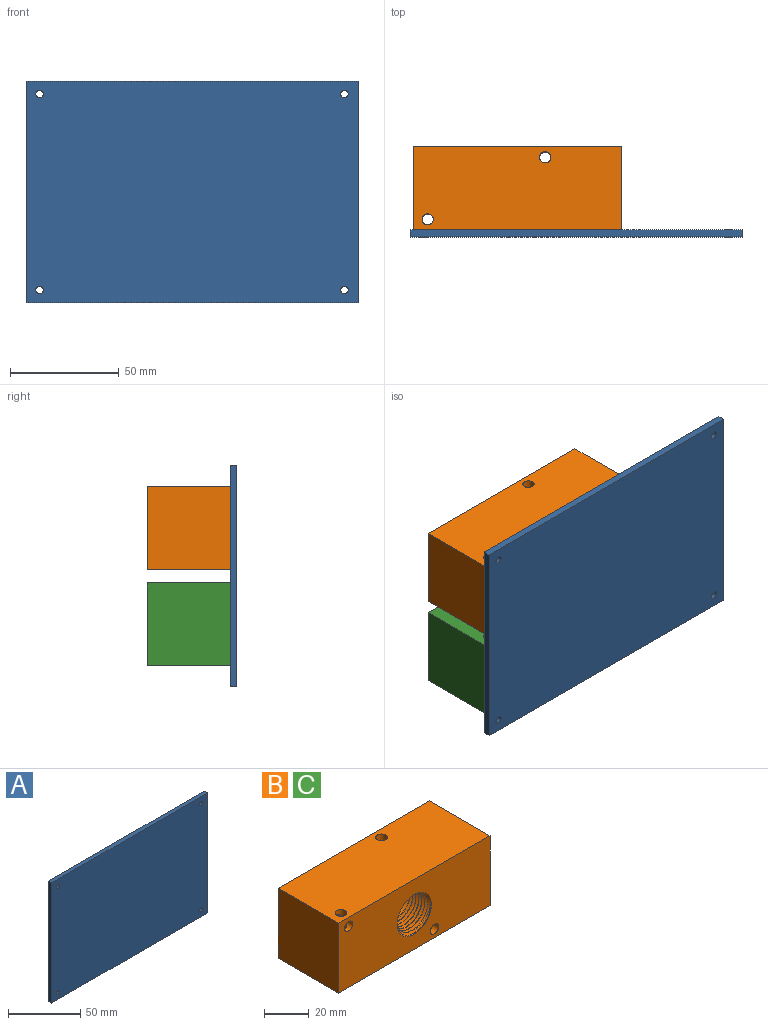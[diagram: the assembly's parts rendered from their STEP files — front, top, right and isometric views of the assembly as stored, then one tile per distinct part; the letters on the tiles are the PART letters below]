
ASSEMBLY  parts=3 mates=1
PART A: 10 faces, bbox 152.4x3.2x101.6 mm
  f0: plane 101.6x3.18mm, normal (1,0,0), area 322.6mm2, adj f1,f3,f4,f5
  f1: plane 152.4x3.18mm, normal (0,0,1), area 483.9mm2, adj f0,f2,f4,f5
  f2: plane 101.6x3.18mm, normal (-1,0,0), area 322.6mm2, adj f1,f3,f4,f5
  f3: plane 152.4x3.18mm, normal (0,0,-1), area 483.9mm2, adj f0,f2,f4,f5
  f4: plane 152.4x101.6mm, normal (0,-1,0), area 15446.4mm2, adj f0,f1,f2,f3,f6,f7,f8,f9
  f5: plane 152.4x101.6mm, normal (0,1,0), area 15446.4mm2, adj f0,f1,f2,f3,f6,f7,f8,f9
  f6: cylinder r=1.73mm len=3.45mm, axis (0,-1,0), area 34.5mm2, adj f4,f5
  f7: cylinder r=1.73mm len=3.45mm, axis (0,-1,0), area 34.5mm2, adj f4,f5
  f8: cylinder r=1.73mm len=3.45mm, axis (0,-1,0), area 34.5mm2, adj f4,f5
  f9: cylinder r=1.73mm len=3.45mm, axis (0,-1,0), area 34.5mm2, adj f4,f5
PART B: 53 faces, bbox 95.3x39.1x38.1 mm
  f0: cylinder r=4.3mm len=8.69mm, axis (0,1,0), area 197.8mm2, adj f17,f36,f52
  f1: cylinder r=4.3mm len=8.69mm, axis (0,1,0), area 160.9mm2, adj f11,f17,f51
  f2: cone r=8.3mm half-angle=45deg, axis (0,1,0), area 57.6mm2, adj f3,f49,f50,f51
  f3: cone r=8.57mm half-angle=1.8deg, axis (0,1,0), area 20.8mm2, adj f2,f4,f49,f50
  f4: cone r=8.83mm half-angle=45deg, axis (0,1,0), area 56.5mm2, adj f3,f5,f35,f49,f50
  f5: cone r=8.83mm half-angle=45deg, axis (0,1,0), area 5.4mm2, adj f4,f49,f50
  f6: cone r=10.79mm half-angle=45deg, axis (0,-1,0), area 58.4mm2, adj f7,f9,f33,f47,f48
  f7: cone r=10.79mm half-angle=45deg, axis (0,-1,0), area 11.3mm2, adj f6,f46,f47,f48
  f8: cone r=10.3mm half-angle=45deg, axis (0,-1,0), area 100.7mm2, adj f9,f45,f46,f47,f48
  f9: cone r=10.67mm half-angle=1.8deg, axis (0,-1,0), area 83mm2, adj f6,f8,f47,f48
  f10: cylinder r=5.89mm len=11.79mm, axis (0,-1,0), area 140.4mm2, adj f11,f17,f43,f44,f45
  f11: cylinder r=4.3mm len=25.4mm, axis (-1,0,0), area 545.2mm2, adj f1,f10,f16,f42,f43,f44
  f12: cone r=8.83mm half-angle=45deg, axis (0,1,0), area 56.5mm2, adj f13,f15,f35,f40,f41
  f13: cone r=8.83mm half-angle=45deg, axis (0,1,0), area 5.4mm2, adj f12,f40,f41
  f14: cone r=8.3mm half-angle=45deg, axis (0,1,0), area 57.6mm2, adj f15,f39,f40,f41
  f15: cone r=8.57mm half-angle=1.8deg, axis (0,1,0), area 20.8mm2, adj f12,f14,f40,f41
  f16: cylinder r=4.3mm len=8.69mm, axis (0,1,0), area 197.8mm2, adj f11,f39,f42
  f17: cylinder r=4.3mm len=25.4mm, axis (-1,0,0), area 545.2mm2, adj f0,f1,f10,f43,f44,f52
  f18: cone r=8.83mm half-angle=45deg, axis (0,1,0), area 56.5mm2, adj f19,f21,f35,f37,f38
  f19: cone r=8.83mm half-angle=45deg, axis (0,1,0), area 5.4mm2, adj f18,f37,f38
  f20: cone r=8.3mm half-angle=45deg, axis (0,1,0), area 57.6mm2, adj f21,f36,f37,f38
  f21: cone r=8.57mm half-angle=1.8deg, axis (0,1,0), area 20.8mm2, adj f18,f20,f37,f38
  f22: cylinder r=2.58mm len=5.16mm, axis (0,1,0), area 57.3mm2, adj f27,f29,f35
  f23: cylinder r=2.58mm len=33.27mm, axis (0,1,0), area 518.1mm2, adj f27,f29,f33
  f24: cylinder r=2.58mm len=33.27mm, axis (0,1,0), area 518.1mm2, adj f26,f28,f35
  f25: cylinder r=2.58mm len=5.16mm, axis (0,1,0), area 57.3mm2, adj f26,f28,f33
  f26: cylinder r=2.58mm len=33.27mm, axis (0,0,-1), area 518.1mm2, adj f24,f25,f31
  f27: cylinder r=2.58mm len=5.16mm, axis (0,0,-1), area 57.3mm2, adj f22,f23,f31
  f28: cylinder r=2.58mm len=5.16mm, axis (0,0,-1), area 57.3mm2, adj f24,f25,f30
  f29: cylinder r=2.58mm len=33.27mm, axis (0,0,-1), area 518.1mm2, adj f22,f23,f30
  f30: plane 95.25x38.1mm, normal (0,0,1), area 3587.3mm2, adj f28,f29,f32,f33,f34,f35
  f31: plane 95.25x38.1mm, normal (0,0,-1), area 3587.3mm2, adj f26,f27,f32,f33,f34,f35
  f32: plane 38.1x38.1mm, normal (-1,0,0), area 1451.6mm2, adj f30,f31,f33,f35
  f33: plane 95.25x38.1mm, normal (0,-1,0), area 3221.2mm2, adj f6,f23,f25,f30,f31,f32,f34
  f34: plane 38.1x38.1mm, normal (1,0,0), area 1451.6mm2, adj f30,f31,f33,f35
  f35: plane 95.25x38.1mm, normal (0,1,0), area 2853mm2, adj f4,f12,f18,f22,f24,f30,f31,f32
  f36: plane 13.68x13.68mm, normal (0,1,0), area 88.9mm2, adj f0,f20
  f37: bspline ~17x16.91mm, area 398.5mm2, adj f18,f19,f20,f21,f38
  f38: bspline ~16.9x16.84mm, area 413.1mm2, adj f18,f19,f20,f21,f37
  f39: plane 13.68x13.68mm, normal (0,1,0), area 88.9mm2, adj f14,f16
  f40: bspline ~17x16.91mm, area 398.5mm2, adj f12,f13,f14,f15,f41
  f41: bspline ~16.9x16.84mm, area 413.1mm2, adj f12,f13,f14,f15,f40
  f42: sphere r=4.3mm, area 58.1mm2, adj f11,f16
  f43: plane 8.06x1.59mm, normal (0,-1,0), area 8.8mm2, adj f10,f11,f17
  f44: plane 8.06x1.59mm, normal (0,-1,0), area 8.8mm2, adj f10,f11,f17
  f45: plane 16.87x16.87mm, normal (0,-1,0), area 114.3mm2, adj f8,f10
  f46: bspline ~18.57x18.55mm, area 83.9mm2, adj f7,f8,f47,f48
  f47: bspline ~21.51x21.51mm, area 537.3mm2, adj f6,f7,f8,f9,f46
  f48: bspline ~21.6x21.59mm, area 560mm2, adj f6,f7,f8,f9,f46
  f49: bspline ~16.9x16.84mm, area 413.1mm2, adj f2,f3,f4,f5,f50
  f50: bspline ~17x16.91mm, area 398.5mm2, adj f2,f3,f4,f5,f49
  f51: plane 13.68x13.68mm, normal (0,1,0), area 88.9mm2, adj f1,f2
  f52: sphere r=4.3mm, area 58.1mm2, adj f0,f17
PART C: same geometry as B
PLACE A at identity fixed
PLACE B t=(-26.8,19.05,22.21)mm
PLACE C t=(-26.8,19.05,-22.24)mm
MATE planar B.f33 <-> A.f5  axis (0,-1,0) through (-26.61,0,22.21)mm
